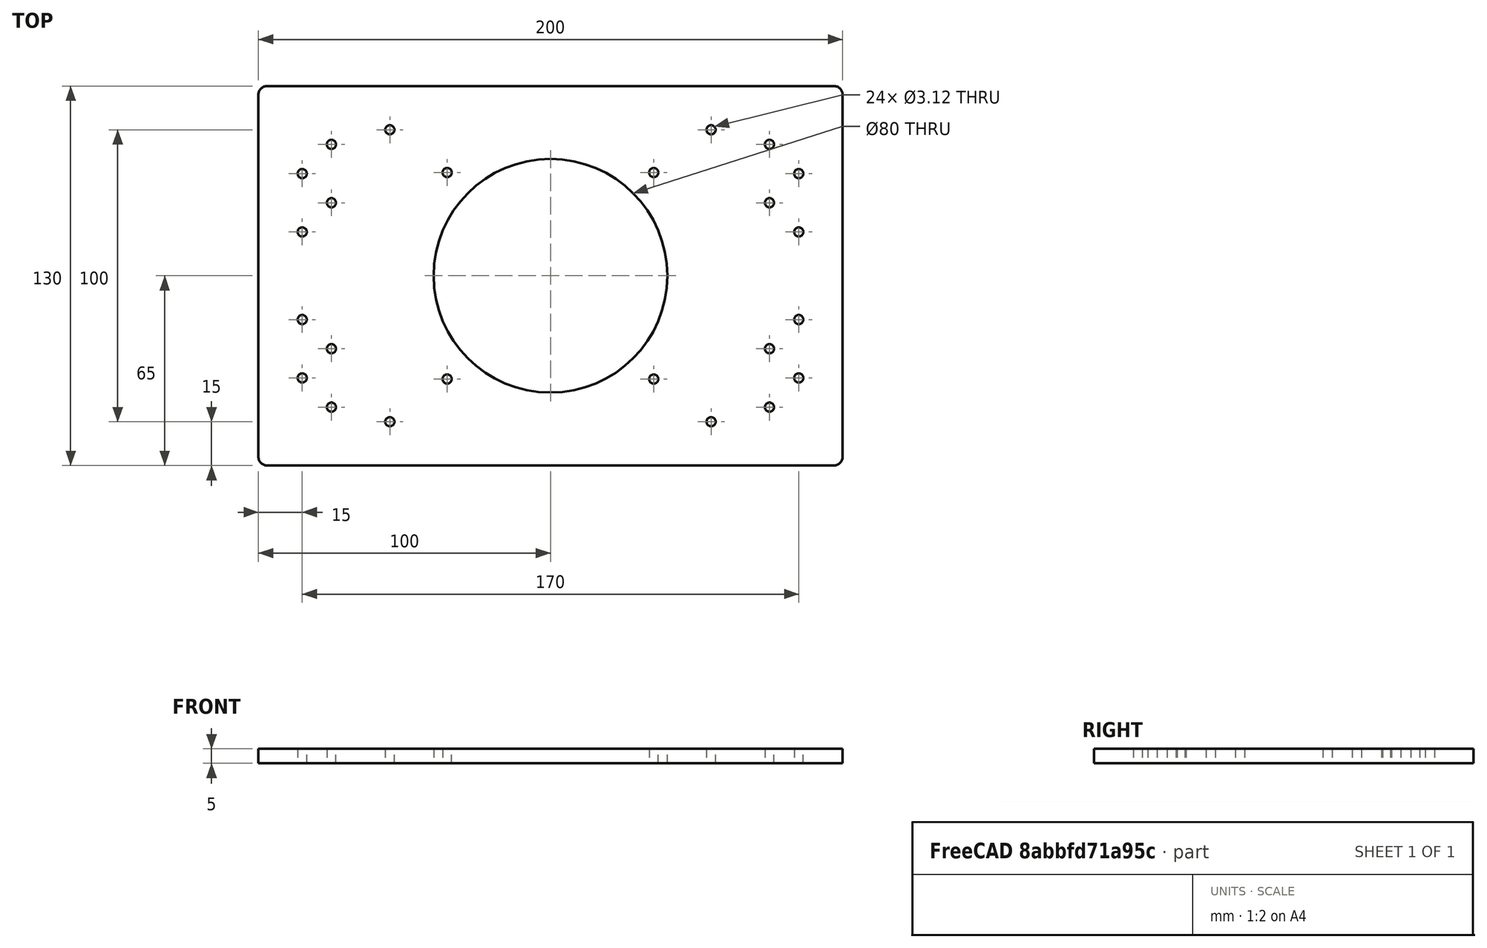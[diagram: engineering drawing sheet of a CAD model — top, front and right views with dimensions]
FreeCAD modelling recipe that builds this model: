
FCSTD DOCUMENT  (FreeCAD 0.19R24276 (Git))
Label: Plate_200x130x5_part4_up_cover
License: All rights reserved
LicenseURL: http://en.wikipedia.org/wiki/All_rights_reserved
objects: Sketcher::SketchObject×1, PartDesign::Pad×1, PartDesign::Fillet×1, PartDesign::Body×1
note: 6 computed .brp shape members not serialized (recipe doc carries the construction recipe); baked Part::Feature solids carry a one-line shape summary decoded from their .brp

FEATURE [Sketcher::SketchObject] Sketch  label="Sketch_d80"
  FullyConstrained = false
  MapMode = 5
  Support = -> [XY_Plane]
  sketch-geometry (44):
    g0: LineSegment StartX=0 StartY=0 StartZ=0 EndX=200 EndY=0 EndZ=0
    g1: LineSegment StartX=200 StartY=0 StartZ=0 EndX=200 EndY=130 EndZ=0
    g2: LineSegment StartX=200 StartY=130 StartZ=0 EndX=0 EndY=130 EndZ=0
    g3: LineSegment StartX=0 StartY=130 StartZ=0 EndX=0 EndY=0 EndZ=0
    g4: Circle CenterX=100 CenterY=65 CenterZ=0 NormalX=0 NormalY=0 NormalZ=1 AngleXU=0 Radius=40
    g5: Circle CenterX=45 CenterY=115 CenterZ=0 NormalX=0 NormalY=0 NormalZ=1 AngleXU=0 Radius=1.5625
    g6: Circle CenterX=45 CenterY=15 CenterZ=0 NormalX=0 NormalY=0 NormalZ=1 AngleXU=0 Radius=1.5625
    g7: Circle CenterX=155 CenterY=115 CenterZ=0 NormalX=0 NormalY=0 NormalZ=1 AngleXU=0 Radius=1.5625
    g8: Circle CenterX=155 CenterY=15 CenterZ=0 NormalX=0 NormalY=0 NormalZ=1 AngleXU=0 Radius=1.5625
    g9: LineSegment StartX=45 StartY=15 StartZ=0 EndX=45 EndY=115 EndZ=0
    g10: LineSegment StartX=45 StartY=15 StartZ=0 EndX=155 EndY=15 EndZ=0
    g11: LineSegment StartX=155 StartY=115 StartZ=0 EndX=155 EndY=15 EndZ=0
    g12: LineSegment StartX=45 StartY=115 StartZ=0 EndX=155 EndY=115 EndZ=0
    g13: Circle CenterX=185 CenterY=30 CenterZ=0 NormalX=0 NormalY=0 NormalZ=1 AngleXU=0 Radius=1.5625
    g14: LineSegment StartX=185 StartY=105 StartZ=0 EndX=185 EndY=30 EndZ=0
    g15: Circle CenterX=99.9949 CenterY=64.986 CenterZ=0 NormalX=0 NormalY=0 NormalZ=1 AngleXU=0 Radius=50
    g16: LineSegment StartX=100 StartY=65 StartZ=0 EndX=135.353 EndY=100.338 EndZ=0
    g17: LineSegment StartX=100 StartY=65 StartZ=0 EndX=64.6278 EndY=29.6424 EndZ=0
    g18: LineSegment StartX=100 StartY=65 StartZ=0 EndX=135.352 EndY=29.6329 EndZ=0
    g19: Circle CenterX=135.353 CenterY=100.338 CenterZ=0 NormalX=0 NormalY=0 NormalZ=1 AngleXU=0 Radius=1.5625
    g20: Circle CenterX=64.6278 CenterY=29.6424 CenterZ=0 NormalX=0 NormalY=0 NormalZ=1 AngleXU=0 Radius=1.5625
    g21: LineSegment StartX=100 StartY=65 StartZ=0 EndX=64.6564 EndY=100.358 EndZ=0
    g22: Circle CenterX=64.6446 CenterY=100.355 CenterZ=0 NormalX=0 NormalY=0 NormalZ=1 AngleXU=0 Radius=1.5625
    g23: Circle CenterX=135.352 CenterY=29.6329 CenterZ=0 NormalX=0 NormalY=0 NormalZ=1 AngleXU=0 Radius=1.5625
    g24: LineSegment StartX=175 StartY=121.301 StartZ=0 EndX=175 EndY=20 EndZ=0
    g25: Circle CenterX=175 CenterY=20 CenterZ=0 NormalX=0 NormalY=0 NormalZ=1 AngleXU=0 Radius=1.5625
    g26: Circle CenterX=175 CenterY=40 CenterZ=0 NormalX=0 NormalY=0 NormalZ=1 AngleXU=0 Radius=1.5625
    g27: Circle CenterX=185 CenterY=50 CenterZ=0 NormalX=0 NormalY=0 NormalZ=1 AngleXU=0 Radius=1.5625
    g28: LineSegment StartX=100 StartY=65 StartZ=0 EndX=228.555 EndY=65 EndZ=0
    g29: Circle CenterX=175 CenterY=90 CenterZ=0 NormalX=0 NormalY=0 NormalZ=1 AngleXU=0 Radius=1.5625
    g30: Circle CenterX=175 CenterY=110 CenterZ=0 NormalX=0 NormalY=0 NormalZ=1 AngleXU=0 Radius=1.5625
    g31: Circle CenterX=185 CenterY=80 CenterZ=0 NormalX=0 NormalY=0 NormalZ=1 AngleXU=0 Radius=1.5625
    g32: Circle CenterX=185 CenterY=100 CenterZ=0 NormalX=0 NormalY=0 NormalZ=1 AngleXU=0 Radius=1.5625
    g33: LineSegment StartX=100 StartY=65 StartZ=0 EndX=100 EndY=146.994 EndZ=0
    g34: Circle CenterX=15 CenterY=30 CenterZ=0 NormalX=0 NormalY=0 NormalZ=1 AngleXU=0 Radius=1.5625
    g35: LineSegment StartX=15 StartY=105 StartZ=0 EndX=15 EndY=30 EndZ=0
    g36: LineSegment StartX=25 StartY=121.301 StartZ=0 EndX=25 EndY=20 EndZ=0
    g37: Circle CenterX=25 CenterY=20 CenterZ=0 NormalX=0 NormalY=0 NormalZ=1 AngleXU=0 Radius=1.5625
    g38: Circle CenterX=25 CenterY=40 CenterZ=0 NormalX=0 NormalY=0 NormalZ=1 AngleXU=0 Radius=1.5625
    g39: Circle CenterX=15 CenterY=50 CenterZ=0 NormalX=0 NormalY=0 NormalZ=1 AngleXU=0 Radius=1.5625
    g40: Circle CenterX=25 CenterY=90 CenterZ=0 NormalX=0 NormalY=0 NormalZ=1 AngleXU=0 Radius=1.5625
    g41: Circle CenterX=25 CenterY=110 CenterZ=0 NormalX=0 NormalY=0 NormalZ=1 AngleXU=0 Radius=1.5625
    g42: Circle CenterX=15 CenterY=80 CenterZ=0 NormalX=0 NormalY=0 NormalZ=1 AngleXU=0 Radius=1.5625
    g43: Circle CenterX=15 CenterY=100 CenterZ=0 NormalX=0 NormalY=0 NormalZ=1 AngleXU=0 Radius=1.5625
  constraints (89):
    c: Coincident(g0,g1)
    c: Coincident(g1,g2)
    c: Coincident(g2,g3)
    c: Coincident(g3,g0)
    c: Horizontal(g0)
    c: Horizontal(g2)
    c: Vertical(g1)
    c: Vertical(g3)
    c: Coincident(g0,g-1)
    c: DistanceY(g1,g1) = 130
    c: DistanceX(g0,g0) = 200
    c: Symmetric(g2,g0,g4)
    c: Diameter(g4) = 80
    c: DistanceX(g0,g6) = 45
    c: Coincident(g9,g6)
    c: Coincident(g9,g5)
    c: Vertical(g9)
    c: Coincident(g10,g6)
    c: Coincident(g10,g8)
    c: Horizontal(g10)
    c: Coincident(g11,g7)
    c: Coincident(g11,g8)
    c: Vertical(g11)
    c: Coincident(g12,g5)
    c: Coincident(g12,g7)
    c: Horizontal(g12)
    c: Symmetric(g7,g6,g4)
    c: DistanceY(g0,g6) = 15
    c: Coincident(g14,g13)
    c: Vertical(g14)
    c: Equal(g5,g6)
    c: Equal(g5,g8)
    c: Equal(g5,g7)
    c: DistanceX(g13,g0) = 15
    c: Diameter(g15) = 100
    c: Coincident(g16,g4)
    c: Coincident(g17,g4)
    c: Coincident(g18,g4)
    c: Parallel(g17,g16)
    c: Angle(g17,g18) = 1.5708
    c: PointOnObject(g18,g15)
    c: PointOnObject(g17,g15)
    c: PointOnObject(g16,g15)
    c: Coincident(g19,g16)
    c: Coincident(g20,g17)
    c: Coincident(g21,g4)
    c: Parallel(g18,g21)
    c: PointOnObject(g21,g15)
    c: Coincident(g23,g18)
    c: Equal(g23,g19)
    c: Equal(g23,g22)
    c: Equal(g23,g20)
    c: Vertical(g24)
    c: DistanceX(g24,g0) = 25
    c: DistanceY(g0,g13) = 30
    c: Coincident(g25,g24)
    c: Equal(g13,g25)
    c: DistanceY(g0,g24) = 20
    c: PointOnObject(g26,g24)
    c: Equal(g25,g26)
    c: DistanceY(g24,g26) = 20
    c: PointOnObject(g27,g14)
    c: Equal(g26,g27)
    c: DistanceY(g13,g27) = 20
    c: Coincident(g28,g4)
    c: Horizontal(g28)
    c: Equal(g32,g30)
    c: Equal(g30,g29)
    c: Equal(g29,g31)
    c: Coincident(g33,g4)
    c: Vertical(g33)
    c: Coincident(g35,g34)
    c: Vertical(g35)
    c: Vertical(g36)
    c: Coincident(g37,g36)
    c: Equal(g34,g37)
    c: PointOnObject(g38,g36)
    c: Equal(g37,g38)
    c: PointOnObject(g39,g35)
    c: Equal(g38,g39)
    c: Equal(g43,g41)
    c: Equal(g41,g40)
    c: Equal(g40,g42)
    c: Diameter(g25) = 3.125
    c: Equal(g25,g31)
    c: Equal(g23,g8)
    c: Equal(g8,g26)
    c: Equal(g37,g42)
    c: Equal(g42,g20)
FEATURE [PartDesign::Pad] Pad  label="Pad_h5"
  Direction = (1,1,1)
  Length = 5
  Length2 = 100
  Profile = -> Sketch
  Type = 0
FEATURE [PartDesign::Fillet] Fillet
  Base = -> Pad [Edge1,Edge2,Edge5,Edge8]
  BaseFeature = -> Pad
  Radius = 3
  SupportTransform = false
FEATURE [PartDesign::Body] Body
  Group = -> [Sketch,Pad,Fillet]
  Origin = -> Origin
  Tip = -> Fillet
